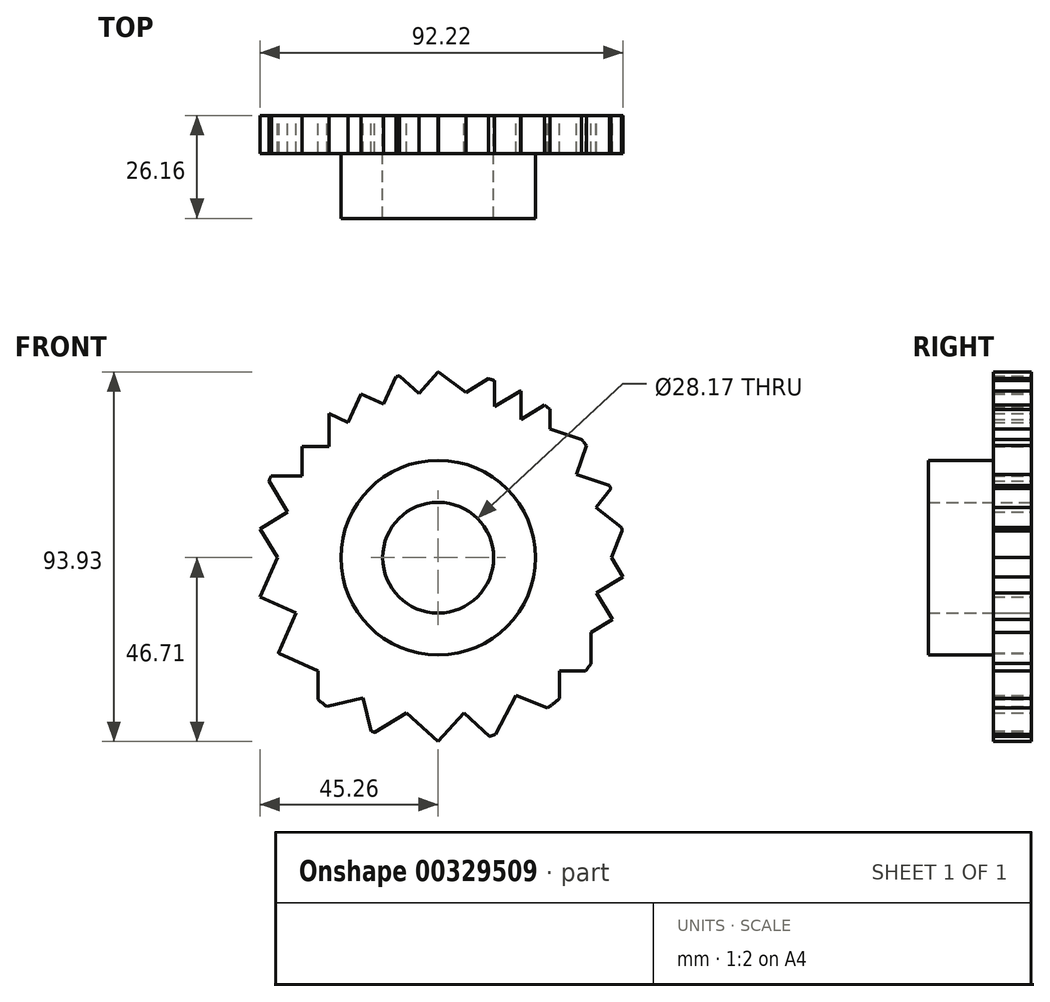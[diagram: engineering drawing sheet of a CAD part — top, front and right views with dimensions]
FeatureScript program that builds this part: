
annotation { "Feature Type Name" : "Feature", "Feature Type Description" : "" }
export const myFeature = defineFeature(function(context is Context, id is Id, definition is map)
    precondition{}
    {
        {
            var Q0;
            Q0=qCreatedBy(makeId("Front.planeOp"),FACE);
            var sketch = newSketch(context, id + "F0", { "sketchPlane" : qUnion([Q0])});
            skCircle(sketch, "E0", {"center": v(0, 0) * mm, "radius": 47.22 * mm});
            skCircle(sketch, "E1", {"center": v(0, 0) * mm, "radius": 26.32 * mm});
            skCircle(sketch, "E2", {"center": v(0, 0) * mm, "radius": 14.08 * mm});
            skSolve(sketch);
        }
        {
            var Q0;
            Q0=makeQuery(id+"F0.imprint","IMPRINT",FACE,{"disambiguationData":[TD([[makeQuery(id+"F0.imprint","IMPRINT",EDGE,{"derivedFrom":sQuery(id+"F0.wireOp",EDGE,"E0")}),1.0]])]});
            var Q1;
            Q1=makeQuery(id+"F0.imprint","IMPRINT",FACE,{"disambiguationData":[TD([[makeQuery(id+"F0.imprint","IMPRINT",EDGE,{"derivedFrom":sQuery(id+"F0.wireOp",EDGE,"E1")}),1.0]])]});
            extrude(context, id + "F1", {"entities" : qUnion([Q0, Q1]), "depth" : 9.65 * mm});
        }
        {
            var Q0;
            Q0=makeQuery(id+"F1.opExtrude","CAP_FACE",FACE,{"disambiguationData":[OSD([sQuery(id+"F0.wireOp",EDGE,"E0"),sQuery(id+"F0.wireOp",EDGE,"E2")])],"isStart":false});
            var sketch = newSketch(context, id + "F2", { "sketchPlane" : qUnion([Q0])});
            skCircle(sketch, "E3", {"center": v(0, 0) * mm, "radius": 24.73 * mm});
            skSolve(sketch);
        }
        {
            var Q0;
            Q0=makeQuery(id+"F2.imprint","IMPRINT",FACE,{"disambiguationData":[TD([[makeQuery(id+"F2.imprint","IMPRINT",EDGE,{"derivedFrom":sQuery(id+"F2.wireOp",EDGE,"E3")}),1.0]])]});
            extrude(context, id + "F3", {"entities" : qUnion([Q0]), "operationType" : NewBodyOperationType.ADD, "depth" : 16.5 * mm});
        }
        {
            var Q0;
            Q0=qCreatedBy(makeId("Front.planeOp"),FACE);
            var sketch = newSketch(context, id + "F4", { "sketchPlane" : qUnion([Q0])});
            skLineSegment(sketch, "E4", {"start": v(0, 47.33) * mm, "end": v(-4.93, 41.78) * mm});
            skLineSegment(sketch, "E5", {"start": v(-4.93, 41.78) * mm, "end": v(-10.39, 46.63) * mm});
            skLineSegment(sketch, "E6", {"start": v(-10.39, 46.63) * mm, "end": v(-13.87, 39) * mm});
            skLineSegment(sketch, "E7", {"start": v(-13.87, 39) * mm, "end": v(-19.56, 41.6) * mm});
            skLineSegment(sketch, "E8", {"start": v(-19.56, 41.6) * mm, "end": v(-22.87, 34.35) * mm});
            skLineSegment(sketch, "E9", {"start": v(-22.87, 34.35) * mm, "end": v(-27.78, 36.6) * mm});
            skLineSegment(sketch, "E10", {"start": v(-27.78, 36.6) * mm, "end": v(-27.78, 28.21) * mm});
            skLineSegment(sketch, "E11", {"start": v(-27.78, 28.21) * mm, "end": v(-34.53, 28.21) * mm});
            skLineSegment(sketch, "E12", {"start": v(-34.53, 28.21) * mm, "end": v(-34.53, 20.81) * mm});
            skLineSegment(sketch, "E13", {"start": v(-34.53, 20.81) * mm, "end": v(-43.78, 20.81) * mm});
            skLineSegment(sketch, "E14", {"start": v(-43.78, 20.81) * mm, "end": v(-38.23, 11.56) * mm});
            skLineSegment(sketch, "E15", {"start": v(-38.23, 11.56) * mm, "end": v(-45.26, 7.35) * mm});
            skLineSegment(sketch, "E16", {"start": v(-45.26, 7.35) * mm, "end": v(-40.85, 0) * mm});
            skLineSegment(sketch, "E17", {"start": v(-40.85, 0) * mm, "end": v(-45.26, -10.02) * mm});
            skLineSegment(sketch, "E18", {"start": v(-45.26, -10.02) * mm, "end": v(-36.1, -14.05) * mm});
            skLineSegment(sketch, "E19", {"start": v(-36.1, -14.05) * mm, "end": v(-40.62, -24.3) * mm});
            skLineSegment(sketch, "E20", {"start": v(-40.62, -24.3) * mm, "end": v(-30.54, -28.73) * mm});
            skLineSegment(sketch, "E21", {"start": v(-30.54, -28.73) * mm, "end": v(-30.54, -38.39) * mm});
            skLineSegment(sketch, "E22", {"start": v(-30.54, -38.39) * mm, "end": v(-19.12, -35.61) * mm});
            skLineSegment(sketch, "E23", {"start": v(-19.12, -35.61) * mm, "end": v(-16.89, -44.78) * mm});
            skLineSegment(sketch, "E24", {"start": v(-16.89, -44.78) * mm, "end": v(-8.04, -39.47) * mm});
            skLineSegment(sketch, "E25", {"start": v(-8.04, -39.47) * mm, "end": v(0, -46.71) * mm});
            skLineSegment(sketch, "E26", {"start": v(0, -46.71) * mm, "end": v(6.52, -39.47) * mm});
            skLineSegment(sketch, "E27", {"start": v(6.52, -39.47) * mm, "end": v(13.9, -46.12) * mm});
            skLineSegment(sketch, "E28", {"start": v(13.9, -46.12) * mm, "end": v(19.73, -35) * mm});
            skLineSegment(sketch, "E29", {"start": v(19.73, -35) * mm, "end": v(30.83, -39.47) * mm});
            skLineSegment(sketch, "E30", {"start": v(30.83, -39.47) * mm, "end": v(30.83, -28.73) * mm});
            skLineSegment(sketch, "E31", {"start": v(30.83, -28.73) * mm, "end": v(38.85, -28.73) * mm});
            skLineSegment(sketch, "E32", {"start": v(38.85, -28.73) * mm, "end": v(38.85, -18.96) * mm});
            skLineSegment(sketch, "E33", {"start": v(38.85, -18.96) * mm, "end": v(44.24, -15.72) * mm});
            skLineSegment(sketch, "E34", {"start": v(44.24, -15.72) * mm, "end": v(40.16, -8.92) * mm});
            skLineSegment(sketch, "E35", {"start": v(40.16, -8.92) * mm, "end": v(46.96, -4.84) * mm});
            skLineSegment(sketch, "E36", {"start": v(46.96, -4.84) * mm, "end": v(44.06, 0) * mm});
            skLineSegment(sketch, "E37", {"start": v(44.06, 0) * mm, "end": v(46.96, 7.35) * mm});
            skLineSegment(sketch, "E38", {"start": v(46.96, 7.35) * mm, "end": v(40.08, 12.8) * mm});
            skLineSegment(sketch, "E39", {"start": v(40.08, 12.8) * mm, "end": v(44.24, 18.05) * mm});
            skLineSegment(sketch, "E40", {"start": v(44.24, 18.05) * mm, "end": v(35.15, 21.12) * mm});
            skLineSegment(sketch, "E41", {"start": v(35.15, 21.12) * mm, "end": v(37.98, 29.52) * mm});
            skLineSegment(sketch, "E42", {"start": v(37.98, 29.52) * mm, "end": v(28.45, 32.74) * mm});
            skLineSegment(sketch, "E43", {"start": v(28.45, 32.74) * mm, "end": v(28.45, 39.62) * mm});
            skLineSegment(sketch, "E44", {"start": v(28.45, 39.62) * mm, "end": v(21, 35.15) * mm});
            skLineSegment(sketch, "E45", {"start": v(21, 35.15) * mm, "end": v(21, 42.4) * mm});
            skLineSegment(sketch, "E46", {"start": v(21, 42.4) * mm, "end": v(14.3, 38.38) * mm});
            skLineSegment(sketch, "E47", {"start": v(14.3, 38.38) * mm, "end": v(14.3, 46.4) * mm});
            skLineSegment(sketch, "E48", {"start": v(14.3, 46.4) * mm, "end": v(7, 42.02) * mm});
            skLineSegment(sketch, "E49", {"start": v(7, 42.02) * mm, "end": v(0, 47.33) * mm});
            skSolve(sketch);
        }
        {
            var Q0;
            Q0=makeQuery(id+"F4.imprint","IMPRINT",FACE,{"disambiguationData":[TD([[makeQuery(id+"F4.imprint","IMPRINT",EDGE,{"derivedFrom":sQuery(id+"F4.wireOp",EDGE,"E4")}),1.0]])]});
            extrude(context, id + "F5", {"entities" : qUnion([Q0]), "operationType" : NewBodyOperationType.INTERSECT, "depth" : 58.17 * mm});
        }
    });
